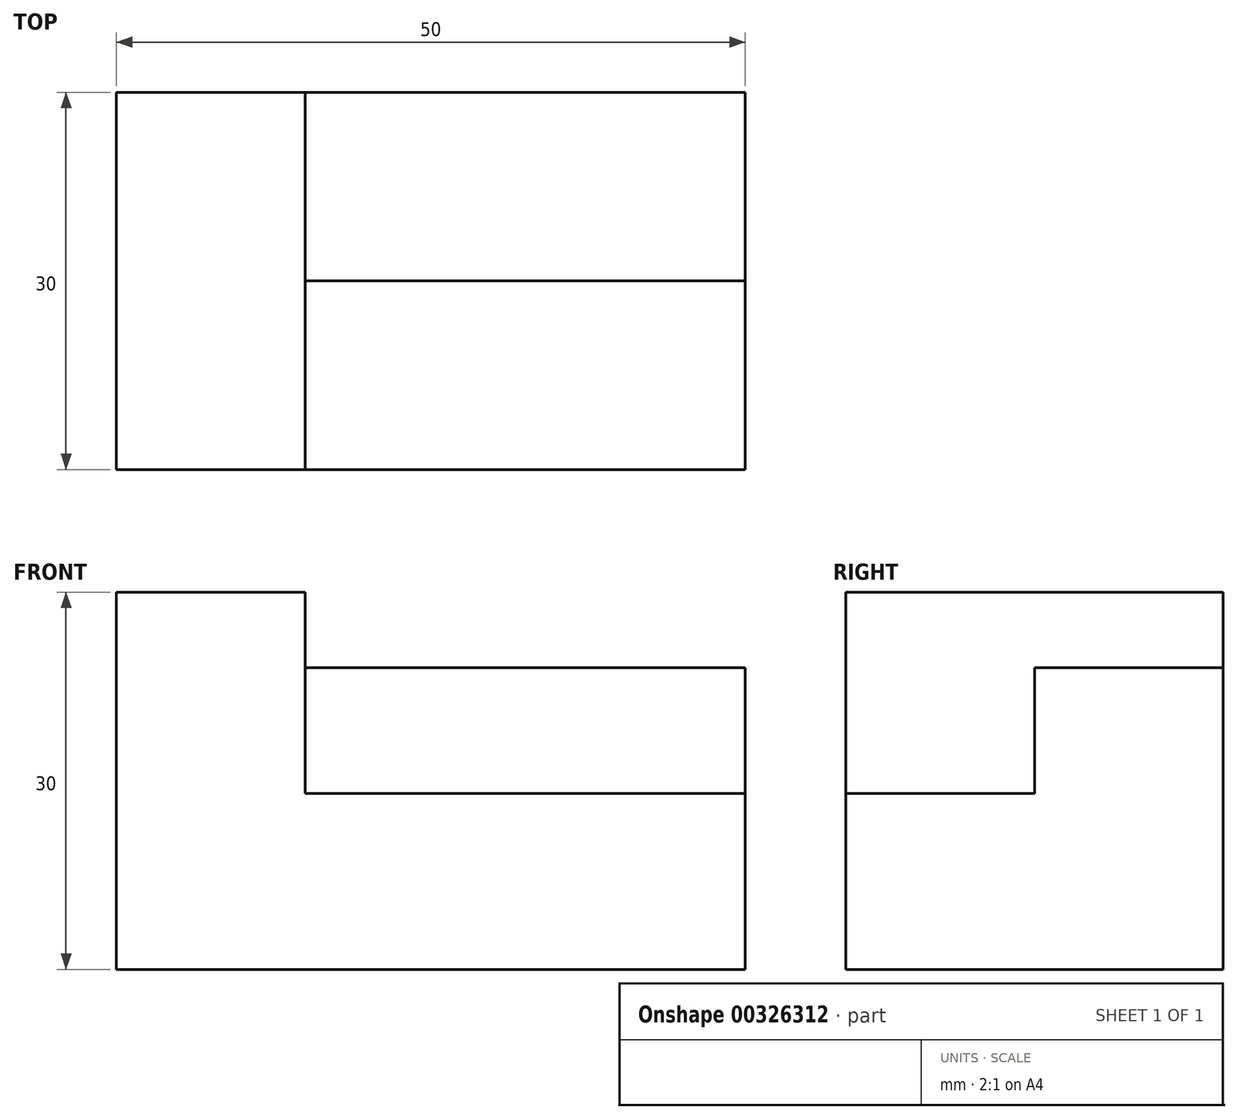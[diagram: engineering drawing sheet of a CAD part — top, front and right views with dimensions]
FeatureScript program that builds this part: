
annotation { "Feature Type Name" : "Feature", "Feature Type Description" : "" }
export const myFeature = defineFeature(function(context is Context, id is Id, definition is map)
    precondition{}
    {
        {
            var Q0;
            Q0=qCreatedBy(makeId("Top.planeOp"),FACE);
            var sketch = newSketch(context, id + "F0", { "sketchPlane" : qUnion([Q0])});
            skLineSegment(sketch, "E0.bottom", {"start": v(0, 0) * mm, "end": v(50, 0) * mm});
            skLineSegment(sketch, "E0.top", {"start": v(0, 30) * mm, "end": v(50, 30) * mm});
            skLineSegment(sketch, "E0.left", {"start": v(0, 0) * mm, "end": v(0, 30) * mm});
            skLineSegment(sketch, "E0.right", {"start": v(50, 0) * mm, "end": v(50, 30) * mm});
            skLineSegment(sketch, "E1", {"start": v(15, 30) * mm, "end": v(15, 0) * mm});
            skLineSegment(sketch, "E2", {"start": v(15, 15) * mm, "end": v(50, 15) * mm});
            skSolve(sketch);
        }
        {
            var Q0;
            Q0 = qSketchRegion(id + "F0", true);
            extrude(context, id + "F1", {"entities" : qUnion([Q0]), "depth" : 14 * mm});
        }
        {
            var Q0;
            {var subQ5=sQuery(id+"F0.wireOp",EDGE,"E2");Q0=makeQuery(id+"F0.imprint","IMPRINT",FACE,{"disambiguationData":[TD([[makeQuery(id+"F0.imprint","IMPRINT",EDGE,{"derivedFrom":subQ5}),1.0]])]});}
            extrude(context, id + "F2", {"entities" : qUnion([Q0]), "operationType" : NewBodyOperationType.ADD, "depth" : 24 * mm});
        }
        {
            var Q0;
            {var subQ0=sQuery(id+"F0.wireOp",EDGE,"E0.left");Q0=makeQuery(id+"F0.imprint","IMPRINT",FACE,{"disambiguationData":[TD([[makeQuery(id+"F0.imprint","IMPRINT",EDGE,{"derivedFrom":subQ0}),-1.0]])]});}
            extrude(context, id + "F3", {"entities" : qUnion([Q0]), "operationType" : NewBodyOperationType.ADD, "depth" : 30 * mm});
        }
    });
